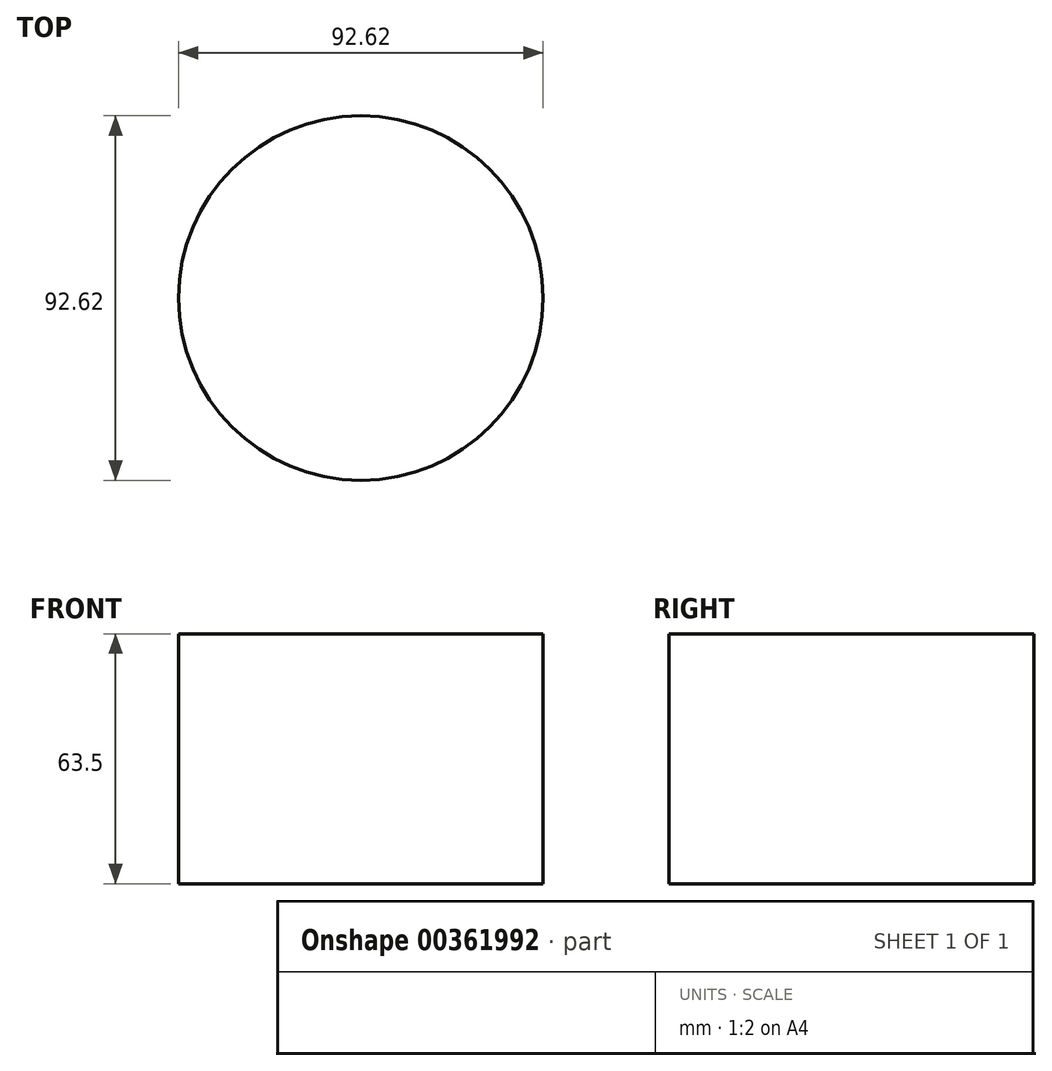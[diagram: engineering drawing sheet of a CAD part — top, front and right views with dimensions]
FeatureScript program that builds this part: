
annotation { "Feature Type Name" : "Feature", "Feature Type Description" : "" }
export const myFeature = defineFeature(function(context is Context, id is Id, definition is map)
    precondition{}
    {
        {
            var Q0;
            Q0=qCreatedBy(makeId("Top.planeOp"),FACE);
            var sketch = newSketch(context, id + "F0", { "sketchPlane" : qUnion([Q0])});
            skCircle(sketch, "E0", {"center": v(0, 0) * mm, "radius": 56.86 * mm});
            skCircle(sketch, "E1", {"center": v(0, 0) * mm, "radius": 46.3 * mm});
            skSolve(sketch);
        }
        {
            var Q0;
            Q0=makeQuery(id+"F0.imprint","IMPRINT",FACE,{"disambiguationData":[TD([[makeQuery(id+"F0.imprint","IMPRINT",EDGE,{"derivedFrom":sQuery(id+"F0.wireOp",EDGE,"E1")}),1.0]])]});
            extrude(context, id + "F1", {"entities" : qUnion([Q0]), "depth" : 63.5 * mm});
        }
    });
